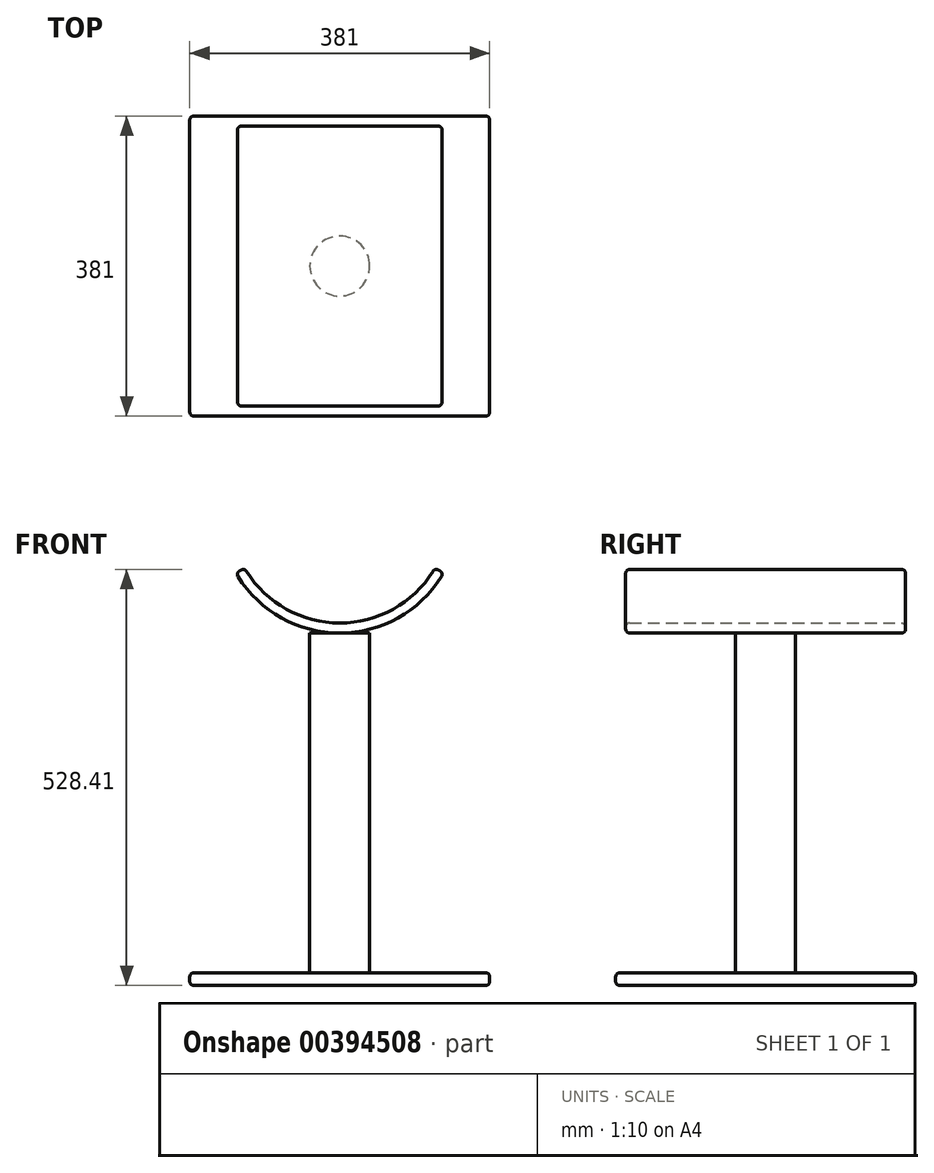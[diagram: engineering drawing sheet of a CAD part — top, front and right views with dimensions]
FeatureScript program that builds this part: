
annotation { "Feature Type Name" : "Feature", "Feature Type Description" : "" }
export const myFeature = defineFeature(function(context is Context, id is Id, definition is map)
    precondition{}
    {
        {
            var Q0;
            Q0=qCreatedBy(makeId("Top.planeOp"),FACE);
            var sketch = newSketch(context, id + "F0", { "sketchPlane" : qUnion([Q0])});
            skLineSegment(sketch, "E0.bottom", {"start": v(190.5, 190.5) * mm, "end": v(-190.5, 190.5) * mm});
            skLineSegment(sketch, "E0.top", {"start": v(190.5, -190.5) * mm, "end": v(-190.5, -190.5) * mm});
            skLineSegment(sketch, "E0.left", {"start": v(190.5, 190.5) * mm, "end": v(190.5, -190.5) * mm});
            skLineSegment(sketch, "E0.right", {"start": v(-190.5, 190.5) * mm, "end": v(-190.5, -190.5) * mm});
            skPoint(sketch, "E0.middle", {"position": v(0, 0) * mm});
            skSolve(sketch);
        }
        {
            var Q0;
            Q0=makeQuery(id+"F0.imprint","IMPRINT",FACE,{"disambiguationData":[TD([[makeQuery(id+"F0.imprint","IMPRINT",EDGE,{"derivedFrom":sQuery(id+"F0.wireOp",EDGE,"E0.bottom")}),1.0]])]});
            extrude(context, id + "F1", {"entities" : qUnion([Q0]), "depth" : 15.88 * mm});
        }
        {
            var Q0;
            Q0=makeQuery(id+"F1.opExtrude","CAP_FACE",FACE,{"disambiguationData":[OSD([sQuery(id+"F0.wireOp",EDGE,"E0.bottom"),sQuery(id+"F0.wireOp",EDGE,"E0.top"),sQuery(id+"F0.wireOp",EDGE,"E0.left"),sQuery(id+"F0.wireOp",EDGE,"E0.right")])],"isStart":false});
            var sketch = newSketch(context, id + "F2", { "sketchPlane" : qUnion([Q0])});
            skCircle(sketch, "E1", {"center": v(0, 0) * mm, "radius": 38.1 * mm});
            skSolve(sketch);
        }
        {
            var Q0;
            Q0=makeQuery(id+"F2.imprint","IMPRINT",FACE,{"disambiguationData":[TD([[makeQuery(id+"F2.imprint","IMPRINT",EDGE,{"derivedFrom":sQuery(id+"F2.wireOp",EDGE,"E1")}),1.0]])]});
            extrude(context, id + "F3", {"entities" : qUnion([Q0]), "depth" : 431.8 * mm});
        }
        {
            var Q0;
            Q0=qCreatedBy(makeId("Front.planeOp"),FACE);
            var sketch = newSketch(context, id + "F4", { "sketchPlane" : qUnion([Q0])});
            skArc(sketch, "E2", {"start": v(-131.98, -76.2) * mm, "mid": v(0, -152.4) * mm, "end": v(131.98, -76.2) * mm});
            skLineSegment(sketch, "E3", {"start": v(0, 0) * mm, "end": v(0, 152.4) * mm, "construction": true});
            skLineSegment(sketch, "E4", {"start": v(0, 0) * mm, "end": v(-131.98, -76.2) * mm, "construction": true});
            skLineSegment(sketch, "E5", {"start": v(0, 0) * mm, "end": v(131.98, -76.2) * mm, "construction": true});
            skArc(sketch, "E6.0", {"start": v(-142.98, -82.55) * mm, "mid": v(0, -165.1) * mm, "end": v(142.98, -82.55) * mm});
            skLineSegment(sketch, "E7", {"start": v(-142.98, -82.55) * mm, "end": v(-131.98, -76.2) * mm});
            skLineSegment(sketch, "E8", {"start": v(131.98, -76.2) * mm, "end": v(142.98, -82.55) * mm});
            skSolve(sketch);
        }
        {
            var Q0;
            Q0=makeQuery(id+"F4.imprint","IMPRINT",FACE,{"disambiguationData":[TD([[makeQuery(id+"F4.imprint","IMPRINT",EDGE,{"derivedFrom":sQuery(id+"F4.wireOp",EDGE,"E2")}),-1.0]])]});
            extrude(context, id + "F5", {"entities" : qUnion([Q0]), "endBound" : BoundingType.SYMMETRIC, "depth" : 355.6 * mm});
        }
        {
            var Q0;
            Q0=makeQuery(id+"F5.opExtrude","CAP_EDGE",EDGE,{"disambiguationData":[OSD([sQuery(id+"F4.wireOp",EDGE,"E8")])],"isStart":false});
            var Q1;
            Q1=makeQuery(id+"F5.opExtrude","CAP_EDGE",EDGE,{"disambiguationData":[OSD([sQuery(id+"F4.wireOp",EDGE,"E8")])],"isStart":true});
            var Q2;
            Q2=makeQuery(id+"F5.opExtrude","CAP_EDGE",EDGE,{"disambiguationData":[OSD([sQuery(id+"F4.wireOp",EDGE,"E7")])],"isStart":true});
            var Q3;
            Q3=makeQuery(id+"F5.opExtrude","CAP_EDGE",EDGE,{"disambiguationData":[OSD([sQuery(id+"F4.wireOp",EDGE,"E7")])],"isStart":false});
            fillet(context, id + "F6", {"entities" : qUnion([Q0, Q1, Q2, Q3]), "radius" : 5.08 * mm, "tangentPropagation" : true, "allowEdgeOverflow" : false});
        }
        {
            var Q0;
            Q0=makeQuery(id+"F5.opExtrude","SWEPT_FACE",FACE,{"disambiguationData":[OSD([sQuery(id+"F4.wireOp",EDGE,"E2")])]});
            var Q1;
            Q1=makeQuery(id+"F5.opExtrude","SWEPT_FACE",FACE,{"disambiguationData":[OSD([sQuery(id+"F4.wireOp",EDGE,"E6.0")])]});
            fillet(context, id + "F7", {"entities" : qUnion([Q0, Q1]), "radius" : 5.08 * mm, "tangentPropagation" : true, "allowEdgeOverflow" : false});
        }
        {
            var Q0;
            Q0=makeQuery(id+"F5.opExtrude","SWEPT_BODY",BODY,{"disambiguationData":[OSD([sQuery(id+"F4.wireOp",EDGE,"E2"),sQuery(id+"F4.wireOp",EDGE,"E6.0"),sQuery(id+"F4.wireOp",EDGE,"E7"),sQuery(id+"F4.wireOp",EDGE,"E8")])]});
            deleteBodies(context, id + "F8", {"entities" : qUnion([Q0])});
        }
        {
            var Q0;
            Q0=qCreatedBy(makeId("Front.planeOp"),FACE);
            var sketch = newSketch(context, id + "F9", { "sketchPlane" : qUnion([Q0])});
            skArc(sketch, "E9", {"start": v(-131.98, 523.88) * mm, "mid": v(0, 447.68) * mm, "end": v(131.98, 523.88) * mm});
            skLineSegment(sketch, "E10", {"start": v(0, 600.08) * mm, "end": v(-131.98, 523.88) * mm, "construction": true});
            skLineSegment(sketch, "E11", {"start": v(0, 600.08) * mm, "end": v(0, 752.48) * mm, "construction": true});
            skLineSegment(sketch, "E12", {"start": v(0, 600.08) * mm, "end": v(131.98, 523.88) * mm, "construction": true});
            skArc(sketch, "E13.0", {"start": v(-120.98, 530.23) * mm, "mid": v(0, 460.38) * mm, "end": v(120.98, 530.23) * mm});
            skLineSegment(sketch, "E14", {"start": v(-120.98, 530.23) * mm, "end": v(-131.98, 523.88) * mm});
            skLineSegment(sketch, "E15", {"start": v(120.98, 530.23) * mm, "end": v(131.98, 523.88) * mm});
            skSolve(sketch);
        }
        {
            var Q0;
            Q0=makeQuery(id+"F9.imprint","IMPRINT",FACE,{"disambiguationData":[TD([[makeQuery(id+"F9.imprint","IMPRINT",EDGE,{"derivedFrom":sQuery(id+"F9.wireOp",EDGE,"E9")}),1.0]])]});
            extrude(context, id + "F10", {"entities" : qUnion([Q0]), "endBound" : BoundingType.SYMMETRIC, "depth" : 355.6 * mm});
        }
        {
            var Q0;
            Q0=makeQuery(id+"F10.opExtrude","CAP_EDGE",EDGE,{"disambiguationData":[OSD([sQuery(id+"F9.wireOp",EDGE,"E15")])],"isStart":false});
            var Q1;
            Q1=makeQuery(id+"F10.opExtrude","CAP_EDGE",EDGE,{"disambiguationData":[OSD([sQuery(id+"F9.wireOp",EDGE,"E14")])],"isStart":false});
            var Q2;
            Q2=makeQuery(id+"F10.opExtrude","CAP_EDGE",EDGE,{"disambiguationData":[OSD([sQuery(id+"F9.wireOp",EDGE,"E15")])],"isStart":true});
            var Q3;
            Q3=makeQuery(id+"F10.opExtrude","CAP_EDGE",EDGE,{"disambiguationData":[OSD([sQuery(id+"F9.wireOp",EDGE,"E14")])],"isStart":true});
            var Q4;
            Q4=makeQuery(id+"F10.opExtrude","SWEPT_FACE",FACE,{"disambiguationData":[OSD([sQuery(id+"F9.wireOp",EDGE,"E13.0")])]});
            var Q5;
            Q5=makeQuery(id+"F10.opExtrude","SWEPT_FACE",FACE,{"disambiguationData":[OSD([sQuery(id+"F9.wireOp",EDGE,"E9")])]});
            fillet(context, id + "F11", {"entities" : qUnion([Q0, Q1, Q2, Q3, Q4, Q5]), "radius" : 5.08 * mm, "tangentPropagation" : true, "allowEdgeOverflow" : false});
        }
        {
            var Q0;
            Q0=makeQuery(id+"F1.opExtrude","SWEPT_EDGE",EDGE,{"disambiguationData":[OSD([sQuery(id+"F0.wireOp",EDGE,"E0.top"),sQuery(id+"F0.wireOp",EDGE,"E0.left")])]});
            var Q1;
            Q1=makeQuery(id+"F1.opExtrude","SWEPT_EDGE",EDGE,{"disambiguationData":[OSD([sQuery(id+"F0.wireOp",EDGE,"E0.bottom"),sQuery(id+"F0.wireOp",EDGE,"E0.left")])]});
            var Q2;
            Q2=makeQuery(id+"F1.opExtrude","SWEPT_EDGE",EDGE,{"disambiguationData":[OSD([sQuery(id+"F0.wireOp",EDGE,"E0.top"),sQuery(id+"F0.wireOp",EDGE,"E0.right")])]});
            var Q3;
            Q3=makeQuery(id+"F1.opExtrude","SWEPT_EDGE",EDGE,{"disambiguationData":[OSD([sQuery(id+"F0.wireOp",EDGE,"E0.bottom"),sQuery(id+"F0.wireOp",EDGE,"E0.right")])]});
            var Q4;
            Q4=makeQuery(id+"F1.opExtrude","CAP_FACE",FACE,{"disambiguationData":[OSD([sQuery(id+"F0.wireOp",EDGE,"E0.bottom"),sQuery(id+"F0.wireOp",EDGE,"E0.top"),sQuery(id+"F0.wireOp",EDGE,"E0.left"),sQuery(id+"F0.wireOp",EDGE,"E0.right")])],"isStart":true});
            var Q5;
            Q5=makeQuery(id+"F1.opExtrude","CAP_FACE",FACE,{"disambiguationData":[OSD([sQuery(id+"F0.wireOp",EDGE,"E0.bottom"),sQuery(id+"F0.wireOp",EDGE,"E0.top"),sQuery(id+"F0.wireOp",EDGE,"E0.left"),sQuery(id+"F0.wireOp",EDGE,"E0.right")])],"isStart":false});
            fillet(context, id + "F12", {"entities" : qUnion([Q0, Q1, Q2, Q3, Q4, Q5]), "radius" : 5.08 * mm, "tangentPropagation" : true, "allowEdgeOverflow" : false});
        }
    });
